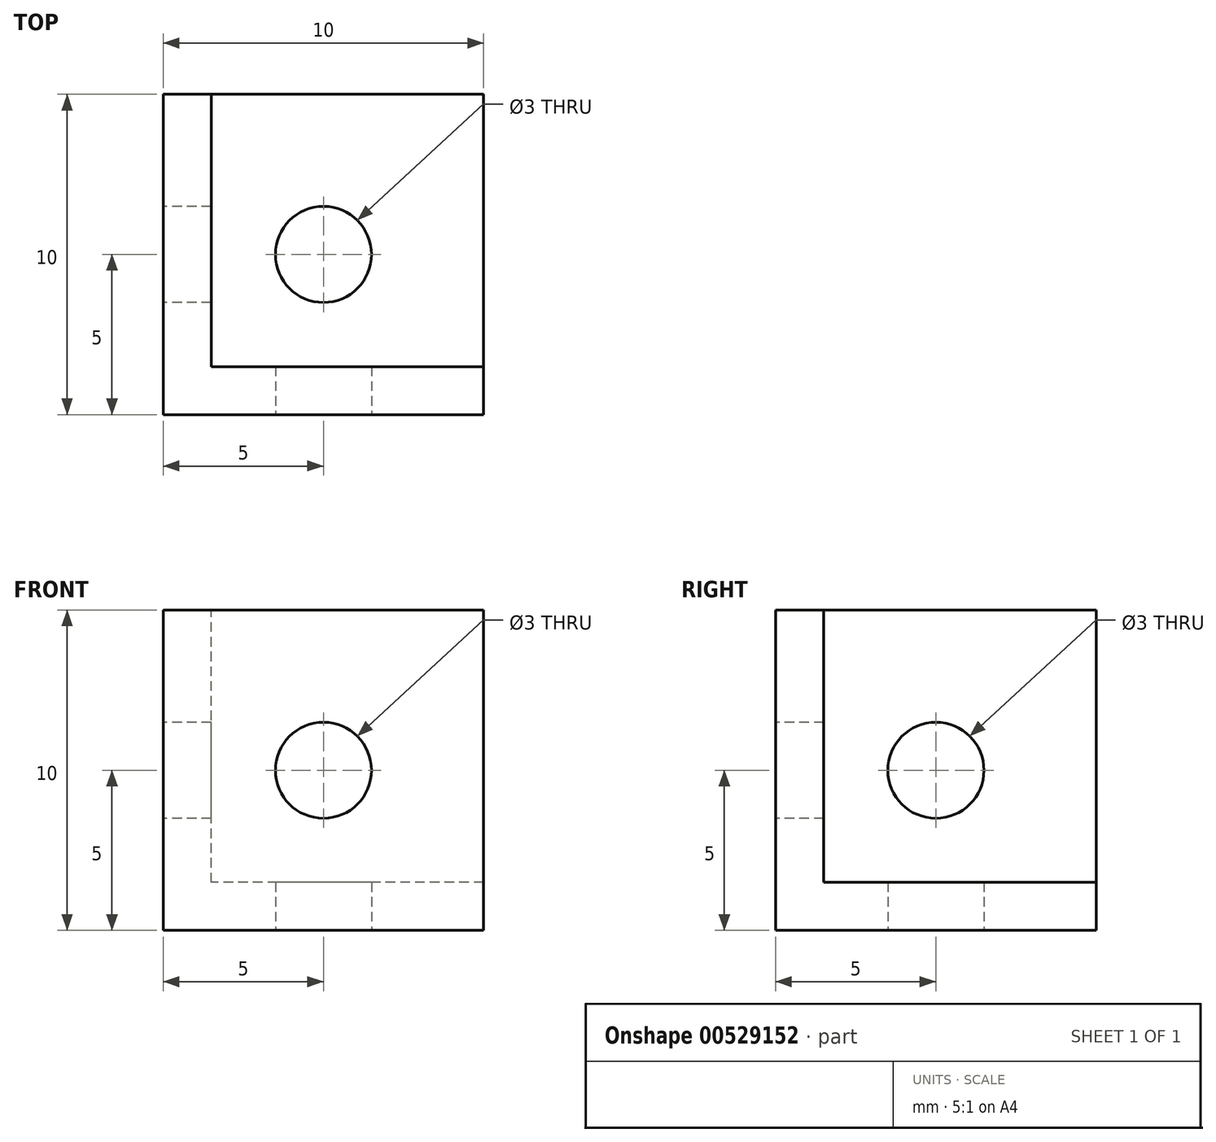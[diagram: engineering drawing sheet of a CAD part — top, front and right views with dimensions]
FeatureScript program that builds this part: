
annotation { "Feature Type Name" : "Feature", "Feature Type Description" : "" }
export const myFeature = defineFeature(function(context is Context, id is Id, definition is map)
    precondition{}
    {
        {
            var Q0;
            Q0=qCreatedBy(makeId("Front.planeOp"),FACE);
            var sketch = newSketch(context, id + "F0", { "sketchPlane" : qUnion([Q0])});
            skLineSegment(sketch, "E0.bottom", {"start": v(10, 0) * mm, "end": v(0, 0) * mm});
            skLineSegment(sketch, "E0.top", {"start": v(10, 10) * mm, "end": v(0, 10) * mm});
            skLineSegment(sketch, "E0.left", {"start": v(10, 0) * mm, "end": v(10, 10) * mm});
            skLineSegment(sketch, "E0.right", {"start": v(0, 0) * mm, "end": v(0, 10) * mm});
            skCircle(sketch, "E1", {"center": v(5, 5) * mm, "radius": 1.5 * mm});
            skSolve(sketch);
        }
        {
            var Q0;
            Q0=qCreatedBy(makeId("Right.planeOp"),FACE);
            var sketch = newSketch(context, id + "F1", { "sketchPlane" : qUnion([Q0])});
            skLineSegment(sketch, "E2.bottom", {"start": v(10, 0) * mm, "end": v(0, 0) * mm});
            skLineSegment(sketch, "E2.top", {"start": v(10, 10) * mm, "end": v(0, 10) * mm});
            skLineSegment(sketch, "E2.left", {"start": v(10, 0) * mm, "end": v(10, 10) * mm});
            skLineSegment(sketch, "E2.right", {"start": v(0, 0) * mm, "end": v(0, 10) * mm});
            skCircle(sketch, "E3", {"center": v(5, 5) * mm, "radius": 1.5 * mm});
            skSolve(sketch);
        }
        {
            var Q0;
            Q0=qCreatedBy(makeId("Top.planeOp"),FACE);
            var sketch = newSketch(context, id + "F2", { "sketchPlane" : qUnion([Q0])});
            skLineSegment(sketch, "E4.bottom", {"start": v(10, 0) * mm, "end": v(0, 0) * mm});
            skLineSegment(sketch, "E4.top", {"start": v(10, 10) * mm, "end": v(0, 10) * mm});
            skLineSegment(sketch, "E4.left", {"start": v(10, 0) * mm, "end": v(10, 10) * mm});
            skLineSegment(sketch, "E4.right", {"start": v(0, 0) * mm, "end": v(0, 10) * mm});
            skCircle(sketch, "E5", {"center": v(5, 5) * mm, "radius": 1.5 * mm});
            skSolve(sketch);
        }
        {
            var Q0;
            Q0 = qSketchRegion(id + "F0", true);
            extrude(context, id + "F3", {"entities" : qUnion([Q0]), "oppositeDirection" : true, "depth" : 1.5 * mm, "offsetDistance" : 25 * mm});
        }
        {
            var Q0;
            Q0=makeQuery(id+"F2.imprint","IMPRINT",FACE,{"disambiguationData":[TD([[makeQuery(id+"F2.imprint","IMPRINT",EDGE,{"derivedFrom":sQuery(id+"F2.wireOp",EDGE,"E4.bottom")}),-1.0]])]});
            extrude(context, id + "F4", {"entities" : qUnion([Q0]), "operationType" : NewBodyOperationType.ADD, "depth" : 1.5 * mm, "offsetDistance" : 25 * mm});
        }
        {
            var Q0;
            Q0=makeQuery(id+"F1.imprint","IMPRINT",FACE,{"disambiguationData":[TD([[makeQuery(id+"F1.imprint","IMPRINT",EDGE,{"derivedFrom":sQuery(id+"F1.wireOp",EDGE,"E2.bottom")}),-1.0]])]});
            extrude(context, id + "F5", {"entities" : qUnion([Q0]), "operationType" : NewBodyOperationType.ADD, "depth" : 1.5 * mm, "offsetDistance" : 25 * mm});
        }
    });
